# Revit family: ROTHOB_Rothoblaas_Screw_LBA
name_source: partatom
category: Structural Connections
units: mm (PartAtom-declared; Revit-internal decimal feet)

## family parameters
Cut with Voids When Loaded = No
Enable cutting in views = Yes
Host = Face
Material for Model Behavior = Steel
OmniClass Number = 23.20.40.11.14.17
OmniClass Title = Nails
Shared = No

## types (9) — shared parameters
AssetType = Fixed
BIMObjectName = ROTHOB_Rothoblaas_Screw_LBA
CECode = ETA-22/0002
CETitle = Rotho Blaas Connector Nails LBA
CodePerformance = CE - Construction products
Color = Silver
Default Elevation = 1219.2 mm
Description = High bond nail
DurationUnit = Years
Esporta tipo in formato IFC con nome = IfcMechanicalFastenerType
ExpectedLife = 50
Features = Adhesion nails with knurled shanks for timber constructions
Finish = Electrogalvanized
IfcExportAs = IfcMechanicalFastenerType
IfcExportType = USERDEFINED
ManufacturerName = ROTHO BLAAS SRL
ManufacturerURL = www.rothoblaas.com
Material = Electrogalvanized carbon steel
ModelDisclaimer = The latest version of the data sheets can be found on our website
Name = Nail
OmniClassCode = 23.20.40.11.14.17
OmniClassTitle = Nails
OmniClassVersion = 2012-05-16
ProductInformation = www.rothoblaas.com/products/fastening/screws/screws-carpentry/lba
Revision = 000
Shape = Cylindrical
Tipo IFC predefinito = USERDEFINED
UniClass2015Version = Products v1.39
Version = 001

## per-type parameters (varying)
| type | Category | ExternalDiameter_de | GTIN | HeadDiameter_dk | HeadThickness_t1 | HoleDiameterOnSteelPlate_dvs | InsertionLength_L | KnurledShanksLength_b | KnurledShanksRadius | MinWeight | ModelNumber | ModelNumberCode | NominalDiameter | NominalDiameter_d1 | NominalLength | ObjectMaterial | ShankLength_Ls | Size | ThreadDiameter_d2 | TipLength_Lt | UnderheadDiameter_d3 | UnderheadLength_L1 | UniClass2015Code | UniClass2015Title |
| LBA440_4x40mm | Pr_20_29_56_11 : Carbon steel nails | 4.4 mm | 8033564765391 | 8 mm  [stored 0.0262467 ft] | 1.5 mm  [stored 0.00492126 ft] | 5.00 ÷5.5 mm | 38.5 mm  [stored 0.126312 ft] | 30 mm  [stored 0.0984252 ft] | 1.7 mm  [stored 0.00557743 ft] | 0.004 kg | LBA440 | 440 | 4 mm  [stored 0.0131234 ft] | 4 mm  [stored 0.0131234 ft] | 40 mm  [stored 0.131234 ft] | ROTHOB_Rothoblaas_CarbonSteel_Electrogalvanized | 6.9 mm  [stored 0.0226378 ft] | 4 x 40 mm | 3.4 mm  [stored 0.0111549 ft] | 3.86 mm  [stored 0.012664 ft] | 5.9 mm  [stored 0.019357 ft] | 1.6 mm  [stored 0.00524934 ft] | Pr_20_29_56_11 | Carbon steel nails |
| LBA450_4x50mm | Pr_20_29_56_11 : Carbon steel nails | 4.4 mm | 8033224488769 | 8 mm  [stored 0.0262467 ft] | 1.5 mm  [stored 0.00492126 ft] | 5.00 ÷5.5 mm | 48.5 mm  [stored 0.159121 ft] | 40 mm  [stored 0.131234 ft] | 1.7 mm  [stored 0.00557743 ft] | 0.005 kg | LBA450 | 450 | 4 mm  [stored 0.0131234 ft] | 4 mm  [stored 0.0131234 ft] | 50 mm  [stored 0.164042 ft] | ROTHOB_Rothoblaas_CarbonSteel_Electrogalvanized | 6.9 mm  [stored 0.0226378 ft] | 4 x 50 mm | 3.4 mm  [stored 0.0111549 ft] | 3.86 mm  [stored 0.012664 ft] | 5.9 mm  [stored 0.019357 ft] | 1.6 mm  [stored 0.00524934 ft] | Pr_20_29_56_11 | Carbon steel nails |
| LBA460_4x60mm | Pr_20_29_56_11 : Carbon steel nails | 4.4 mm | 8033224488776 | 8 mm  [stored 0.0262467 ft] | 1.5 mm  [stored 0.00492126 ft] | 5.00 ÷5.5 mm | 58.5 mm  [stored 0.191929 ft] | 50 mm  [stored 0.164042 ft] | 1.7 mm  [stored 0.00557743 ft] | 0.006 kg | LBA460 | 460 | 4 mm  [stored 0.0131234 ft] | 4 mm  [stored 0.0131234 ft] | 60 mm  [stored 0.19685 ft] | ROTHOB_Rothoblaas_CarbonSteel_Electrogalvanized | 6.9 mm  [stored 0.0226378 ft] | 4 x 60 mm | 3.4 mm  [stored 0.0111549 ft] | 3.86 mm  [stored 0.012664 ft] | 5.9 mm  [stored 0.019357 ft] | 1.6 mm  [stored 0.00524934 ft] | Pr_20_29_56_11 | Carbon steel nails |
| LBA475_4x75mm | Pr_20_29_56_11 : Carbon steel nails | 4.4 mm | 8033564765407 | 8 mm  [stored 0.0262467 ft] | 1.5 mm  [stored 0.00492126 ft] | 5.00 ÷5.5 mm | 73.5 mm  [stored 0.241142 ft] | 65 mm  [stored 0.213255 ft] | 1.7 mm  [stored 0.00557743 ft] | 0.008 kg | LBA475 | 475 | 4 mm  [stored 0.0131234 ft] | 4 mm  [stored 0.0131234 ft] | 75 mm | ROTHOB_Rothoblaas_CarbonSteel_Electrogalvanized | 6.9 mm  [stored 0.0226378 ft] | 4 x 75 mm | 3.4 mm  [stored 0.0111549 ft] | 3.86 mm  [stored 0.012664 ft] | 5.9 mm  [stored 0.019357 ft] | 1.6 mm  [stored 0.00524934 ft] | Pr_20_29_56_11 | Carbon steel nails |
| LBA4100_4x100mm | Pr_20_29_56_11 : Carbon steel nails | 4.4 mm | 8033564765414 | 8 mm  [stored 0.0262467 ft] | 1.5 mm  [stored 0.00492126 ft] | 5.00 ÷5.5 mm | 98.5 mm | 85 mm  [stored 0.278871 ft] | 1.7 mm  [stored 0.00557743 ft] | 0.010 kg | LBA4100 | 4100 | 4 mm  [stored 0.0131234 ft] | 4 mm  [stored 0.0131234 ft] | 100 mm  [stored 0.328084 ft] | ROTHOB_Rothoblaas_CarbonSteel_Electrogalvanized | 11.9 mm  [stored 0.039042 ft] | 4 x 100 mm | 3.4 mm  [stored 0.0111549 ft] | 3.86 mm  [stored 0.012664 ft] | 5.9 mm  [stored 0.019357 ft] | 1.6 mm  [stored 0.00524934 ft] | Pr_20_29_56_11 | Carbon steel nails |
| LBA660_6x60mm | Pr_20_29_56_11 : Carbon steel nails | 6.6 mm  [stored 0.0216535 ft] | 8033564765421 | 12 mm  [stored 0.0393701 ft] | 2 mm  [stored 0.00656168 ft] | 7.00 ÷7.5 mm | 58 mm  [stored 0.190289 ft] | 50 mm  [stored 0.164042 ft] | 2.75 mm  [stored 0.00902231 ft] | 0.014 kg | LBA660 | 660 | 6 mm  [stored 0.019685 ft] | 6 mm  [stored 0.019685 ft] | 60 mm  [stored 0.19685 ft] | ROTHOB_Rothoblaas_CarbonSteel_Electrogalvanized | 5.15 mm | 6 x 60 mm | 5.5 mm  [stored 0.0180446 ft] | 6.68 mm  [stored 0.021916 ft] | 7.8 mm  [stored 0.0255906 ft] | 2.85 mm  [stored 0.00935039 ft] | Pr_20_29_56_11 | Carbon steel nails |
| LBA680_6x80mm | Pr_20_29_56_11 : Carbon steel nails | 6.6 mm  [stored 0.0216535 ft] | 8033564765438 | 12 mm  [stored 0.0393701 ft] | 2 mm  [stored 0.00656168 ft] | 7.00 ÷7.5 mm | 78 mm  [stored 0.255906 ft] | 70 mm  [stored 0.229659 ft] | 2.75 mm  [stored 0.00902231 ft] | 0.019 kg | LBA680 | 680 | 6 mm  [stored 0.019685 ft] | 6 mm  [stored 0.019685 ft] | 80 mm  [stored 0.262467 ft] | ROTHOB_Rothoblaas_CarbonSteel_Electrogalvanized | 5.15 mm | 6 x 80 mm | 5.5 mm  [stored 0.0180446 ft] | 6.68 mm  [stored 0.021916 ft] | 7.8 mm  [stored 0.0255906 ft] | 2.85 mm  [stored 0.00935039 ft] | Pr_20_29_56_11 | Carbon steel nails |
| LBA6100_6x100mm | Pr_20_29_56_11 : Carbon steel nails | 6.6 mm  [stored 0.0216535 ft] | 8033564765445 | 12 mm  [stored 0.0393701 ft] | 2 mm  [stored 0.00656168 ft] | 7.00 ÷7.5 mm | 98 mm  [stored 0.321522 ft] | 85 mm  [stored 0.278871 ft] | 2.75 mm  [stored 0.00902231 ft] | 0.023 kg | LBA6100 | 6100 | 6 mm  [stored 0.019685 ft] | 6 mm  [stored 0.019685 ft] | 100 mm  [stored 0.328084 ft] | ROTHOB_Rothoblaas_CarbonSteel_Electrogalvanized | 10.15 mm  [stored 0.0333005 ft] | 6 x 100 mm | 5.5 mm  [stored 0.0180446 ft] | 6.68 mm  [stored 0.021916 ft] | 7.8 mm  [stored 0.0255906 ft] | 2.85 mm  [stored 0.00935039 ft] | Pr_20_29_56_11 | Carbon steel nails |
| LBAI450_4x50mm | Pr_20_29_56_85 : Stainless steel nails | 4.4 mm | 8033564764417 | 8 mm  [stored 0.0262467 ft] | 1.5 mm  [stored 0.00492126 ft] | 5.00 ÷5.5 mm | 48.5 mm  [stored 0.159121 ft] | 40 mm  [stored 0.131234 ft] | 1.7 mm  [stored 0.00557743 ft] | 0.005 kg | LBAI450 | 451 | 4 mm  [stored 0.0131234 ft] | 4 mm  [stored 0.0131234 ft] | 50 mm  [stored 0.164042 ft] | ROTHOB_Rothoblaas_StainlessSteel_A4 | 6.9 mm  [stored 0.0226378 ft] | 4 x 50 mm | 3.4 mm  [stored 0.0111549 ft] | 3.86 mm  [stored 0.012664 ft] | 5.9 mm  [stored 0.019357 ft] | 1.6 mm  [stored 0.00524934 ft] | Pr_20_29_56_85 | Stainless steel nails |

note: [stored X ft] marks values corroborated as IEEE doubles in the binary element streams (Revit-internal decimal feet)
